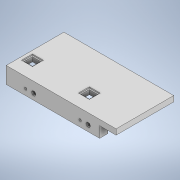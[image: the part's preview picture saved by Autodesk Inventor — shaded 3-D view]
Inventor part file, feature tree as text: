
AUTODESK INVENTOR PART (.ipt)
format: ipt  version: 2020 (Build 240168000, 168)  size: 269,824 bytes
history: native  units: mm
features: sketch x8, extrude x7, projected_geometry x7, other x2, hole x1
ambient origin geometry x8: Origin, YZ Plane, XZ Plane, XY Plane, X Axis, Y Axis, Z Axis, Center Point
bodies: Body1 (feature_tree)
feature tree (25):
  other  "작업 평면1"
  sketch  "스케치1"
  extrude  "돌출1"  Depth=15.0mm TaperAngle=0.0deg
  extrude  "돌출2"  Depth=40.0mm
  extrude  "돌출3"  Depth=230.0mm
  hole  "구멍1"  [1 undecoded]
  extrude  "돌출4"  Depth=7.456mm
  extrude  "돌출5"  Depth=7.456mm
  extrude  "돌출6"  Depth=15.0mm
  extrude  "돌출7"  Depth=19.0mm
  sketch  "스케치2"
  projected_geometry  "투영된 루프2"
  sketch  "스케치3"
  sketch  "스케치4"
  projected_geometry  "투영된 루프3"
  sketch  "스케치5"
  projected_geometry  "투영된 루프4"
  sketch  "스케치6"
  projected_geometry  "투영된 루프5"
  sketch  "스케치7"
  projected_geometry  "투영된 루프6"
  projected_geometry  "투영된 루프7"
  sketch  "스케치8"
  projected_geometry  "투영된 루프8"
  other  "솔리드1"
note: 1 required parameter value undecoded (feature->parameter linkage not recoverable at this tier; creation-order binding heuristic only, values carry confidence <= 0.55)
